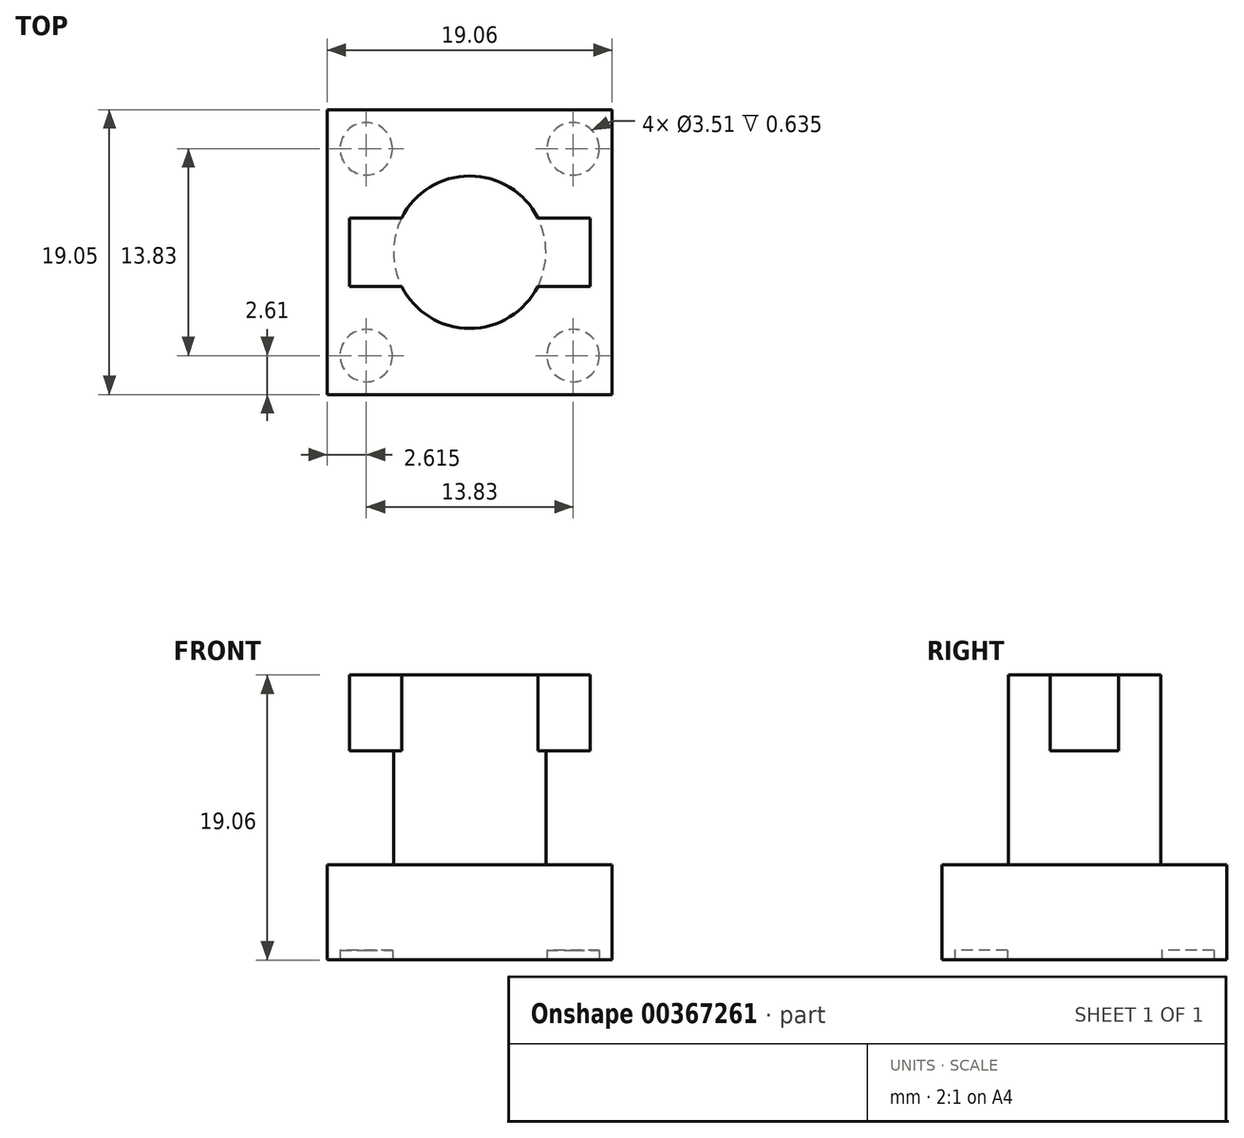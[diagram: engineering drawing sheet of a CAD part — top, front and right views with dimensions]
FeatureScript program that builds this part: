
annotation { "Feature Type Name" : "Feature", "Feature Type Description" : "" }
export const myFeature = defineFeature(function(context is Context, id is Id, definition is map)
    precondition{}
    {
        {
            var Q0;
            Q0=qCreatedBy(makeId("Front.planeOp"),FACE);
            var sketch = newSketch(context, id + "F0", { "sketchPlane" : qUnion([Q0])});
            skCircle(sketch, "E0", {"center": v(0, 0) * mm, "radius": 5.1 * mm});
            skSolve(sketch);
        }
        {
            var Q0;
            Q0=makeQuery(id+"F0.imprint","IMPRINT",FACE,{"disambiguationData":[TD([[makeQuery(id+"F0.imprint","IMPRINT",EDGE,{"derivedFrom":sQuery(id+"F0.wireOp",EDGE,"E0")}),1.0]])]});
            extrude(context, id + "F1", {"entities" : qUnion([Q0]), "depth" : 12.7 * mm});
        }
        {
            var Q0;
            Q0=makeQuery(id+"F1.opExtrude","CAP_FACE",FACE,{"disambiguationData":[OSD([sQuery(id+"F0.wireOp",EDGE,"E0")])],"isStart":false});
            var sketch = newSketch(context, id + "F2", { "sketchPlane" : qUnion([Q0])});
            skLineSegment(sketch, "E1", {"start": v(-4.56, 2.29) * mm, "end": v(-8.05, 2.29) * mm});
            skLineSegment(sketch, "E2", {"start": v(-8.05, 2.29) * mm, "end": v(-8.05, -2.29) * mm});
            skLineSegment(sketch, "E3", {"start": v(-8.05, -2.29) * mm, "end": v(-4.56, -2.29) * mm});
            skLineSegment(sketch, "E4", {"start": v(4.56, 2.29) * mm, "end": v(8.05, 2.29) * mm});
            skLineSegment(sketch, "E5", {"start": v(8.05, 2.29) * mm, "end": v(8.05, -2.29) * mm});
            skLineSegment(sketch, "E6", {"start": v(8.05, -2.29) * mm, "end": v(4.56, -2.29) * mm});
            skSolve(sketch);
        }
        {
            var Q0;
            {var subQ0=sQuery(id+"F2.wireOp",EDGE,"E1");Q0=makeQuery(id+"F2.imprint","IMPRINT",FACE,{"disambiguationData":[TD([[makeQuery(id+"F2.imprint","IMPRINT",EDGE,{"derivedFrom":subQ0}),1.0]])]});}
            var Q1;
            {var subQ0=sQuery(id+"F2.wireOp",EDGE,"E4");Q1=makeQuery(id+"F2.imprint","IMPRINT",FACE,{"disambiguationData":[TD([[makeQuery(id+"F2.imprint","IMPRINT",EDGE,{"derivedFrom":subQ0}),-1.0]])]});}
            extrude(context, id + "F3", {"entities" : qUnion([Q0, Q1]), "operationType" : NewBodyOperationType.ADD, "oppositeDirection" : true, "depth" : 5.08 * mm});
        }
        {
            var Q0;
            Q0=qCreatedBy(makeId("Front.planeOp"),FACE);
            var sketch = newSketch(context, id + "F4", { "sketchPlane" : qUnion([Q0])});
            skLineSegment(sketch, "E7.bottom", {"start": v(-9.52, -9.53) * mm, "end": v(9.53, -9.53) * mm});
            skLineSegment(sketch, "E7.top", {"start": v(-9.53, 9.52) * mm, "end": v(9.52, 9.52) * mm});
            skLineSegment(sketch, "E7.left", {"start": v(-9.52, -9.53) * mm, "end": v(-9.53, 9.52) * mm});
            skLineSegment(sketch, "E7.right", {"start": v(9.53, -9.53) * mm, "end": v(9.52, 9.52) * mm});
            skPoint(sketch, "E7.middle", {"position": v(0, 0) * mm});
            skSolve(sketch);
        }
        {
            var Q0;
            Q0=qSketchRegion(id+"F4",true);
            extrude(context, id + "F5", {"entities" : qUnion([Q0]), "operationType" : NewBodyOperationType.ADD, "oppositeDirection" : true, "depth" : 6.35 * mm});
        }
        {
            var Q0;
            Q0=makeQuery(id+"F5.opExtrude","CAP_FACE",FACE,{"disambiguationData":[OSD([sQuery(id+"F4.wireOp",EDGE,"E7.bottom"),sQuery(id+"F4.wireOp",EDGE,"E7.top"),sQuery(id+"F4.wireOp",EDGE,"E7.left"),sQuery(id+"F4.wireOp",EDGE,"E7.right")])],"isStart":false});
            var sketch = newSketch(context, id + "F6", { "sketchPlane" : qUnion([Q0])});
            skPoint(sketch, "E8.middle", {"position": v(0, 0) * mm});
            skCircle(sketch, "E9", {"center": v(-6.92, 6.92) * mm, "radius": 1.75 * mm});
            skCircle(sketch, "E10", {"center": v(6.92, -6.92) * mm, "radius": 1.75 * mm});
            skCircle(sketch, "E11", {"center": v(-6.92, -6.92) * mm, "radius": 1.75 * mm});
            skLineSegment(sketch, "E12.bottom", {"start": v(-6.92, 6.92) * mm, "end": v(6.92, 6.92) * mm});
            skLineSegment(sketch, "E12.top", {"start": v(-6.92, -6.92) * mm, "end": v(6.92, -6.92) * mm});
            skLineSegment(sketch, "E12.left", {"start": v(-6.92, 6.92) * mm, "end": v(-6.92, -6.92) * mm});
            skLineSegment(sketch, "E12.right", {"start": v(6.92, 6.92) * mm, "end": v(6.92, -6.92) * mm});
            skCircle(sketch, "E13", {"center": v(6.92, 6.92) * mm, "radius": 1.75 * mm});
            skSolve(sketch);
        }
        {
            var Q0;
            {var subQ0=sQuery(id+"F6.wireOp",EDGE,"E12.bottom");var subQ1=sQuery(id+"F6.wireOp",EDGE,"E9");var subQ2=makeQuery(id+"F6.imprint","INTERSECT",VERTEX,{"derivedFrom":[subQ1,subQ0]});Q0=makeQuery(id+"F6.imprint","IMPRINT",FACE,{"disambiguationData":[TD([[makeQuery(id+"F6.imprint","IMPRINT",EDGE,{"disambiguationData":[TD([[subQ2,-1.0]])],"derivedFrom":subQ1}),1.0]])]});}
            var Q1;
            {var subQ0=sQuery(id+"F6.wireOp",EDGE,"E12.bottom");var subQ1=sQuery(id+"F6.wireOp",EDGE,"E9");var subQ2=makeQuery(id+"F6.imprint","INTERSECT",VERTEX,{"derivedFrom":[subQ1,subQ0]});Q1=makeQuery(id+"F6.imprint","IMPRINT",FACE,{"disambiguationData":[TD([[makeQuery(id+"F6.imprint","IMPRINT",EDGE,{"disambiguationData":[TD([[subQ2,1.0]])],"derivedFrom":subQ1}),1.0]])]});}
            var Q2;
            {var subQ0=sQuery(id+"F6.wireOp",EDGE,"E12.right");var subQ1=sQuery(id+"F6.wireOp",EDGE,"E12.bottom");var subQ2=makeQuery(id+"F6.imprint","INTERSECT",VERTEX,{"derivedFrom":[subQ1,subQ0]});Q2=makeQuery(id+"F6.imprint","IMPRINT",FACE,{"disambiguationData":[TD([[makeQuery(id+"F6.imprint","IMPRINT",EDGE,{"disambiguationData":[TD([[subQ2,1.0]])],"derivedFrom":subQ1}),1.0]])]});}
            var Q3;
            {var subQ0=sQuery(id+"F6.wireOp",EDGE,"E12.right");var subQ1=sQuery(id+"F6.wireOp",EDGE,"E12.bottom");var subQ2=makeQuery(id+"F6.imprint","INTERSECT",VERTEX,{"derivedFrom":[subQ1,subQ0]});Q3=makeQuery(id+"F6.imprint","IMPRINT",FACE,{"disambiguationData":[TD([[makeQuery(id+"F6.imprint","IMPRINT",EDGE,{"disambiguationData":[TD([[subQ2,1.0]])],"derivedFrom":subQ1}),-1.0]])]});}
            var Q4;
            {var subQ0=sQuery(id+"F6.wireOp",EDGE,"E12.top");var subQ1=sQuery(id+"F6.wireOp",EDGE,"E10");var subQ2=makeQuery(id+"F6.imprint","INTERSECT",VERTEX,{"derivedFrom":[subQ1,subQ0]});Q4=makeQuery(id+"F6.imprint","IMPRINT",FACE,{"disambiguationData":[TD([[makeQuery(id+"F6.imprint","IMPRINT",EDGE,{"disambiguationData":[TD([[subQ2,1.0]])],"derivedFrom":subQ1}),1.0]])]});}
            var Q5;
            {var subQ0=sQuery(id+"F6.wireOp",EDGE,"E12.top");var subQ1=sQuery(id+"F6.wireOp",EDGE,"E10");var subQ2=makeQuery(id+"F6.imprint","INTERSECT",VERTEX,{"derivedFrom":[subQ1,subQ0]});Q5=makeQuery(id+"F6.imprint","IMPRINT",FACE,{"disambiguationData":[TD([[makeQuery(id+"F6.imprint","IMPRINT",EDGE,{"disambiguationData":[TD([[subQ2,-1.0]])],"derivedFrom":subQ1}),1.0]])]});}
            var Q6;
            {var subQ0=sQuery(id+"F6.wireOp",EDGE,"E12.top");var subQ1=sQuery(id+"F6.wireOp",EDGE,"E11");var subQ2=makeQuery(id+"F6.imprint","INTERSECT",VERTEX,{"derivedFrom":[subQ1,subQ0]});Q6=makeQuery(id+"F6.imprint","IMPRINT",FACE,{"disambiguationData":[TD([[makeQuery(id+"F6.imprint","IMPRINT",EDGE,{"disambiguationData":[TD([[subQ2,-1.0]])],"derivedFrom":subQ1}),1.0]])]});}
            var Q7;
            {var subQ0=sQuery(id+"F6.wireOp",EDGE,"E12.top");var subQ1=sQuery(id+"F6.wireOp",EDGE,"E11");var subQ2=makeQuery(id+"F6.imprint","INTERSECT",VERTEX,{"derivedFrom":[subQ1,subQ0]});Q7=makeQuery(id+"F6.imprint","IMPRINT",FACE,{"disambiguationData":[TD([[makeQuery(id+"F6.imprint","IMPRINT",EDGE,{"disambiguationData":[TD([[subQ2,1.0]])],"derivedFrom":subQ1}),1.0]])]});}
            extrude(context, id + "F7", {"entities" : qUnion([Q0, Q1, Q2, Q3, Q4, Q5, Q6, Q7]), "operationType" : NewBodyOperationType.REMOVE, "oppositeDirection" : true, "depth" : 0.64 * mm});
        }
        {
            var Q0;
            Q0=makeQuery(id+"F1.opExtrude","SWEPT_BODY",BODY,{"disambiguationData":[OSD([sQuery(id+"F0.wireOp",EDGE,"E0")])]});
            var Q1;
            Q1=makeQuery(id+"F5.opExtrude","CAP_EDGE",EDGE,{"disambiguationData":[OSD([sQuery(id+"F4.wireOp",EDGE,"E7.bottom")])],"isStart":false});
            transform(context, id + "F8", {"entities" : qUnion([Q0]), "transformType" : TransformType.ROTATION, "transformAxis" : qUnion([Q1]), "angle" : 90 * degree, "oppositeDirection" : true, "makeCopy" : false});
        }
    });
